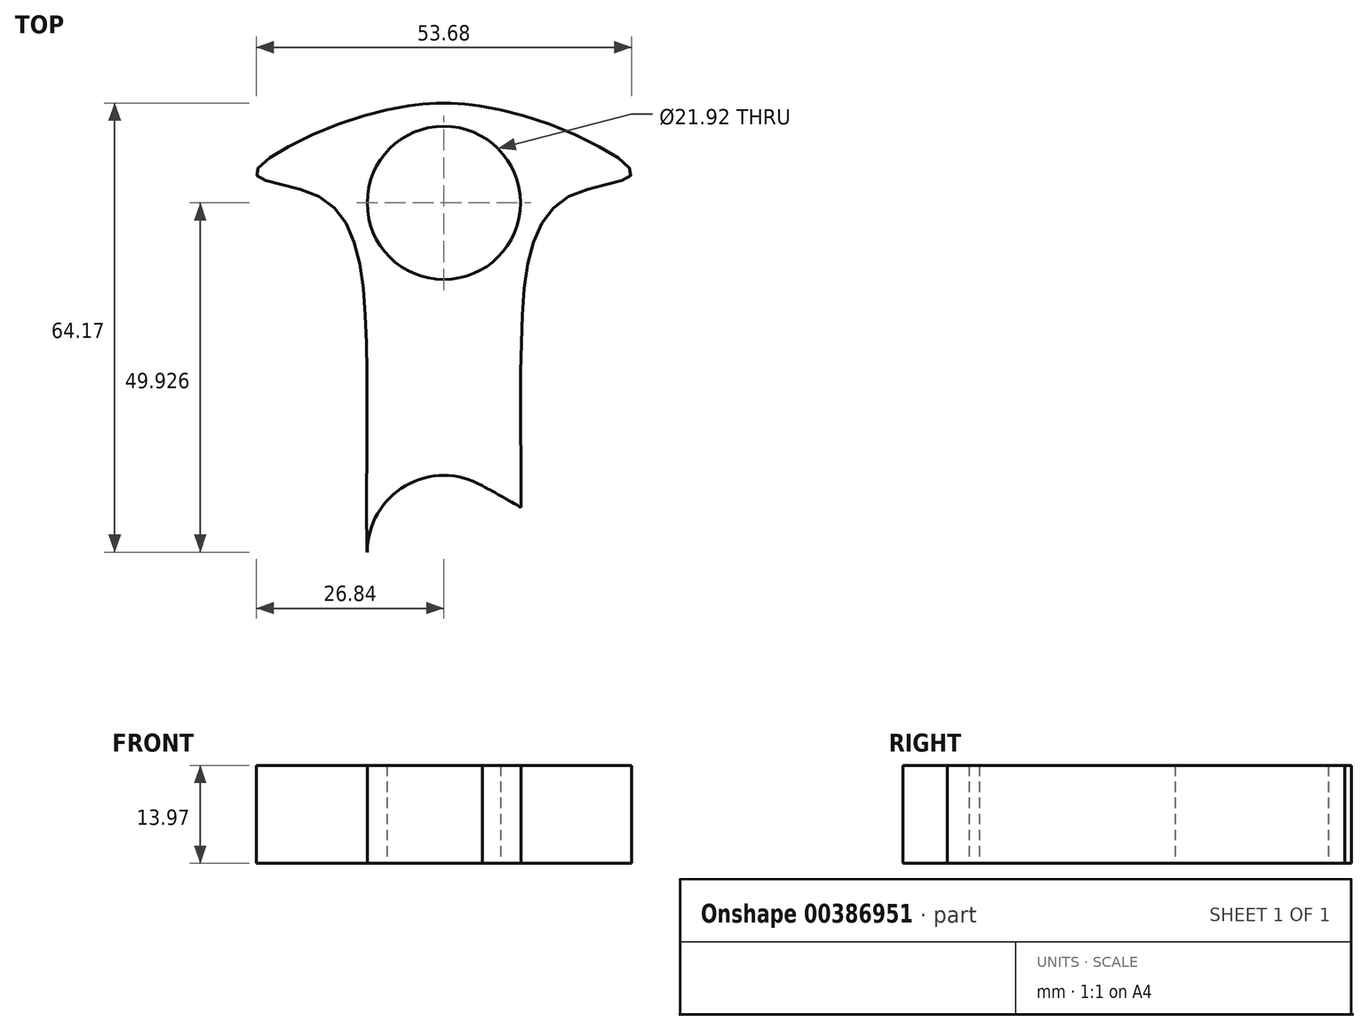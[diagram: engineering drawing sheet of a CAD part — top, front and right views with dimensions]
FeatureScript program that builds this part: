
annotation { "Feature Type Name" : "Feature", "Feature Type Description" : "" }
export const myFeature = defineFeature(function(context is Context, id is Id, definition is map)
    precondition{}
    {
        {
            var Q0;
            Q0=qCreatedBy(makeId("Top.planeOp"),FACE);
            var sketch = newSketch(context, id + "F0", { "sketchPlane" : qUnion([Q0])});
            skPoint(sketch, "E0.center", {"position": v(0, 0) * mm});
            skPoint(sketch, "E1.orphan", {"position": v(10.96, 0) * mm});
            skFitSpline(sketch, "E2", {"points": [v(-10.96, 0) * mm, v(-11.1, 30.9) * mm, v(-17.4, 50.57) * mm, v(-26.84, 54.25) * mm, v(-8.12, 63.2) * mm], "startDerivative": vector(-2.56, 70.78) * mm, "endDerivative": vector(75.6, 12.47) * mm});
            skFitSpline(sketch, "E3.MirrorCS", {"points": [v(10.96, 0) * mm, v(11.1, 30.9) * mm, v(17.4, 50.57) * mm, v(26.84, 54.25) * mm, v(8.12, 63.2) * mm], "startDerivative": vector(2.56, 70.78) * mm, "endDerivative": vector(-75.6, 12.47) * mm});
            skCircle(sketch, "E4", {"center": v(0, 49.93) * mm, "radius": 10.96 * mm});
            skCircle(sketch, "E5", {"center": v(0, 0) * mm, "radius": 10.96 * mm});
            skFitSpline(sketch, "E6", {"points": [v(5.47, -9.5) * mm, v(-21.22, -25.08) * mm, v(-35.1, -40.36) * mm, v(-33.57, -50.37) * mm, v(-50.68, -38.63) * mm], "startDerivative": vector(-60.02, -37.6) * mm, "endDerivative": vector(-48.6, 59.23) * mm});
            skFitSpline(sketch, "E7.MirrorCS", {"points": [v(-5.5, 9.49) * mm, v(-32.33, -5.84) * mm, v(-52.5, -10.22) * mm, v(-60.4, -3.88) * mm, v(-58.8, -24.57) * mm], "startDerivative": vector(-62.58, -33.18) * mm, "endDerivative": vector(27, -71.7) * mm});
            skCircle(sketch, "E8", {"center": v(-43.25, -24.97) * mm, "radius": 10.96 * mm});
            skFitSpline(sketch, "E9", {"points": [v(5.48, 9.49) * mm, v(32.32, -5.84) * mm, v(52.5, -10.22) * mm, v(60.4, -3.88) * mm, v(58.79, -24.57) * mm], "startDerivative": vector(62.58, -33.18) * mm, "endDerivative": vector(-27, -71.7) * mm});
            skFitSpline(sketch, "E10.MirrorCS", {"points": [v(-5.48, -9.5) * mm, v(21.21, -25.07) * mm, v(35.1, -40.36) * mm, v(33.56, -50.37) * mm, v(50.67, -38.63) * mm], "startDerivative": vector(60.02, -37.6) * mm, "endDerivative": vector(48.6, 59.23) * mm});
            skCircle(sketch, "E11", {"center": v(43.24, -24.96) * mm, "radius": 10.96 * mm});
            skLineSegment(sketch, "E12", {"start": v(11.05, 6.38) * mm, "end": v(11.05, 6.38) * mm});
            skArc(sketch, "E13", {"start": v(8.12, 63.2) * mm, "mid": v(0, 64.17) * mm, "end": v(-8.12, 63.2) * mm});
            skArc(sketch, "E14", {"start": v(50.67, -38.63) * mm, "mid": v(55.59, -32.1) * mm, "end": v(58.79, -24.57) * mm});
            skArc(sketch, "E15", {"start": v(-58.8, -24.57) * mm, "mid": v(-55.57, -32.09) * mm, "end": v(-50.68, -38.63) * mm});
            skPoint(sketch, "E16.visualSharp", {"position": v(-11.05, 6.38) * mm});
            skArc(sketch, "E16.filletArc", {"start": v(-13.56, 4.92) * mm, "mid": v(-11.72, 6.77) * mm, "end": v(-11.04, 9.28) * mm});
            skPoint(sketch, "E17.visualSharp", {"position": v(0, -12.76) * mm});
            skArc(sketch, "E17.filletArc", {"start": v(2.52, -14.2) * mm, "mid": v(0, -13.53) * mm, "end": v(-2.52, -14.2) * mm});
            skArc(sketch, "E18.filletArc", {"start": v(11.04, 9.28) * mm, "mid": v(11.72, 6.77) * mm, "end": v(13.56, 4.92) * mm});
            skSolve(sketch);
        }
        {
            var Q0;
            Q0=makeQuery(id+"F0.imprint","IMPRINT",FACE,{"disambiguationData":[TD([[makeQuery(id+"F0.imprint","IMPRINT",EDGE,{"derivedFrom":sQuery(id+"F0.wireOp",EDGE,"E2")}),-1.0]])]});
            extrude(context, id + "F1", {"entities" : qUnion([Q0]), "depth" : 13.97 * mm});
        }
    });
